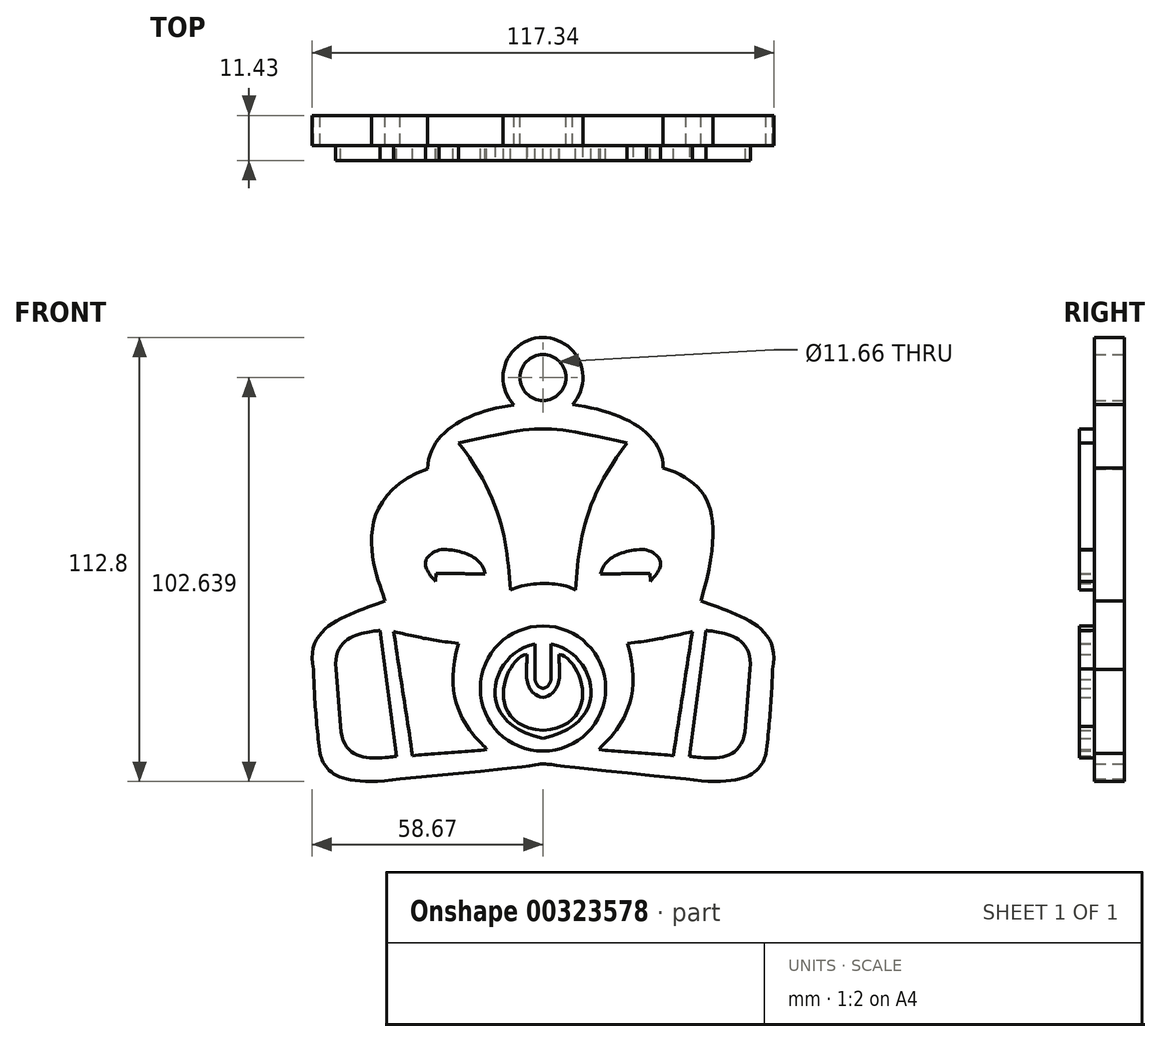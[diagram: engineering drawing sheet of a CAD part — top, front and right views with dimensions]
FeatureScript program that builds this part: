
annotation { "Feature Type Name" : "Feature", "Feature Type Description" : "" }
export const myFeature = defineFeature(function(context is Context, id is Id, definition is map)
    precondition{}
    {
        {
            var Q0;
            Q0=qCreatedBy(makeId("Front.planeOp"),FACE);
            var sketch = newSketch(context, id + "F0", { "sketchPlane" : qUnion([Q0])});
            skFitSpline(sketch, "E0", {"points": [v(-40.16, -4.93) * mm, v(-29.28, 28.6) * mm], "startDerivative": vector(-4.08, 14.8) * mm, "endDerivative": vector(66.61, 24.47) * mm});
            skFitSpline(sketch, "E1", {"points": [v(-29.28, 28.6) * mm, v(30.53, 28.82) * mm], "startDerivative": vector(1.44, 68.84) * mm, "endDerivative": vector(-0.6, -63.84) * mm});
            skFitSpline(sketch, "E2", {"points": [v(30.53, 28.82) * mm, v(40.16, -4.93) * mm], "startDerivative": vector(36.03, -11.56) * mm, "endDerivative": vector(-19.45, -66.97) * mm});
            skFitSpline(sketch, "E3", {"points": [v(-40.16, -4.93) * mm, v(-58.33, -22.39) * mm], "startDerivative": vector(-21.75, -9.52) * mm, "endDerivative": vector(7.92, -36) * mm});
            skFitSpline(sketch, "E4", {"points": [v(-56.66, -43.75) * mm, v(-58.33, -22.39) * mm], "startDerivative": vector(-2.72, 21.98) * mm, "endDerivative": vector(-0.72, 22.32) * mm});
            skFitSpline(sketch, "E5", {"points": [v(-56.66, -43.75) * mm, v(-36.3, -50.25) * mm], "startDerivative": vector(3.4, -12.91) * mm, "endDerivative": vector(48.26, 6.8) * mm});
            skFitSpline(sketch, "E6.MirrorCS", {"points": [v(56.66, -43.75) * mm, v(58.33, -22.39) * mm], "startDerivative": vector(2.72, 21.98) * mm, "endDerivative": vector(0.72, 22.32) * mm});
            skFitSpline(sketch, "E7.MirrorCS", {"points": [v(40.16, -4.93) * mm, v(58.33, -22.39) * mm], "startDerivative": vector(21.75, -9.52) * mm, "endDerivative": vector(-7.92, -36) * mm});
            skFitSpline(sketch, "E8.MirrorCS", {"points": [v(56.66, -43.75) * mm, v(36.3, -50.25) * mm], "startDerivative": vector(-3.4, -12.91) * mm, "endDerivative": vector(-48.26, 6.8) * mm});
            skFitSpline(sketch, "E9", {"points": [v(-36.3, -50.25) * mm, v(0, -46.4) * mm, v(36.3, -50.25) * mm], "startDerivative": vector(202.74, 18.7) * mm, "endDerivative": vector(201.98, -20.2) * mm});
            skSolve(sketch);
        }
        {
            var Q0;
            Q0=qSketchRegion(id+"F0",true);
            extrude(context, id + "F1", {"entities" : qUnion([Q0]), "depth" : 7.62 * mm});
        }
        {
            var Q0;
            Q0=makeQuery(id+"F1.opExtrude","CAP_FACE",FACE,{"disambiguationData":[OSD([sQuery(id+"F0.wireOp",EDGE,"E0"),sQuery(id+"F0.wireOp",EDGE,"E1"),sQuery(id+"F0.wireOp",EDGE,"E2"),sQuery(id+"F0.wireOp",EDGE,"E3"),sQuery(id+"F0.wireOp",EDGE,"E4"),sQuery(id+"F0.wireOp",EDGE,"E5"),sQuery(id+"F0.wireOp",EDGE,"E6.MirrorCS"),sQuery(id+"F0.wireOp",EDGE,"E7.MirrorCS"),sQuery(id+"F0.wireOp",EDGE,"E8.MirrorCS"),sQuery(id+"F0.wireOp",EDGE,"E9")])],"isStart":false});
            var sketch = newSketch(context, id + "F2", { "sketchPlane" : qUnion([Q0])});
            skFitSpline(sketch, "E10", {"points": [v(-8.3, -2.17) * mm, v(-21.4, 35.12) * mm], "startDerivative": vector(-2.34, 34.98) * mm, "endDerivative": vector(-33.95, 43.65) * mm});
            skFitSpline(sketch, "E11.MirrorCS", {"points": [v(8.3, -2.17) * mm, v(21.4, 35.12) * mm], "startDerivative": vector(2.34, 34.98) * mm, "endDerivative": vector(33.95, 43.65) * mm});
            skFitSpline(sketch, "E12", {"points": [v(-21.4, 35.12) * mm, v(21.4, 35.12) * mm], "startDerivative": vector(64.2, 14.53) * mm, "endDerivative": vector(64.2, -14.53) * mm});
            skFitSpline(sketch, "E13", {"points": [v(-8.3, -2.17) * mm, v(8.3, -2.17) * mm], "startDerivative": vector(15.24, 6.52) * mm, "endDerivative": vector(12.2, -6.52) * mm});
            skFitSpline(sketch, "E14", {"points": [v(-37.93, -12.75) * mm, v(-33.13, -44.31) * mm], "startDerivative": vector(4.8, -31.93) * mm, "endDerivative": vector(4.8, -31.93) * mm});
            skFitSpline(sketch, "E15", {"points": [v(-33.13, -44.31) * mm, v(-14.28, -42.75) * mm], "startDerivative": vector(16.8, 1.92) * mm, "endDerivative": vector(16.8, 1.92) * mm});
            skFitSpline(sketch, "E16", {"points": [v(-37.93, -12.75) * mm, v(-21.48, -15.75) * mm], "startDerivative": vector(18.72, -4.32) * mm, "endDerivative": vector(21.6, -2.16) * mm});
            skFitSpline(sketch, "E17", {"points": [v(-14.28, -42.75) * mm, v(-21.48, -15.75) * mm], "startDerivative": vector(-3.24, 6.12) * mm, "endDerivative": vector(15.84, 54.01) * mm});
            skFitSpline(sketch, "E18.MirrorCS", {"points": [v(37.93, -12.75) * mm, v(33.13, -44.31) * mm], "startDerivative": vector(-4.8, -31.93) * mm, "endDerivative": vector(-4.8, -31.93) * mm});
            skFitSpline(sketch, "E19.MirrorCS", {"points": [v(37.93, -12.75) * mm, v(21.48, -15.75) * mm], "startDerivative": vector(-18.72, -4.32) * mm, "endDerivative": vector(-21.6, -2.16) * mm});
            skFitSpline(sketch, "E20.MirrorCS", {"points": [v(14.28, -42.75) * mm, v(21.48, -15.75) * mm], "startDerivative": vector(3.24, 6.12) * mm, "endDerivative": vector(-15.84, 54.01) * mm});
            skFitSpline(sketch, "E21.MirrorCS", {"points": [v(33.13, -44.31) * mm, v(14.28, -42.75) * mm], "startDerivative": vector(-16.8, 1.92) * mm, "endDerivative": vector(-16.8, 1.92) * mm});
            skCircle(sketch, "E22", {"center": v(0, -27.23) * mm, "radius": 15.9 * mm});
            skFitSpline(sketch, "E23", {"points": [v(-2.08, -15.9) * mm, v(0, -39.95) * mm], "startDerivative": vector(-32.37, -5.93) * mm, "endDerivative": vector(56.75, -12.7) * mm});
            skFitSpline(sketch, "E24.MirrorCS", {"points": [v(2.08, -15.9) * mm, v(0, -39.95) * mm], "startDerivative": vector(32.37, -5.93) * mm, "endDerivative": vector(-56.75, -12.7) * mm});
            skFitSpline(sketch, "E25", {"points": [v(-27.26, 0) * mm, v(-26.36, 8) * mm], "startDerivative": vector(-11.06, 11.33) * mm, "endDerivative": vector(13.49, 5.4) * mm});
            skFitSpline(sketch, "E26", {"points": [v(-26.36, 8) * mm, v(-14.67, 1.89) * mm], "startDerivative": vector(14.03, 1.08) * mm, "endDerivative": vector(2.43, -14.03) * mm});
            skFitSpline(sketch, "E27", {"points": [v(-27.17, 1.98) * mm, v(-14.67, 1.89) * mm], "startDerivative": vector(11.42, -0.18) * mm, "endDerivative": vector(11.42, -0.18) * mm});
            skFitSpline(sketch, "E28", {"points": [v(-27.26, 0) * mm, v(-27.17, 1.98) * mm], "startDerivative": vector(0.09, 1.98) * mm, "endDerivative": vector(0.09, 1.98) * mm});
            skFitSpline(sketch, "E29.MirrorCS", {"points": [v(27.17, 1.98) * mm, v(14.67, 1.89) * mm], "startDerivative": vector(-11.42, -0.18) * mm, "endDerivative": vector(-11.42, -0.18) * mm});
            skFitSpline(sketch, "E30.MirrorCS", {"points": [v(27.26, 0) * mm, v(26.36, 8) * mm], "startDerivative": vector(11.06, 11.33) * mm, "endDerivative": vector(-13.49, 5.4) * mm});
            skFitSpline(sketch, "E31.MirrorCS", {"points": [v(26.36, 8) * mm, v(14.67, 1.89) * mm], "startDerivative": vector(-14.03, 1.08) * mm, "endDerivative": vector(-2.43, -14.03) * mm});
            skFitSpline(sketch, "E32.MirrorCS", {"points": [v(27.26, 0) * mm, v(27.17, 1.98) * mm], "startDerivative": vector(-0.09, 1.98) * mm, "endDerivative": vector(-0.09, 1.98) * mm});
            skFitSpline(sketch, "E33", {"points": [v(-4.05, -18.57) * mm, v(0, -37.94) * mm], "startDerivative": vector(-17, -2.38) * mm, "endDerivative": vector(47.17, -4.42) * mm});
            skFitSpline(sketch, "E34", {"points": [v(-4.05, -18.57) * mm, v(0, -29.56) * mm], "startDerivative": vector(0.34, -9.86) * mm, "endDerivative": vector(16.92, -4.08) * mm});
            skFitSpline(sketch, "E35.MirrorCS", {"points": [v(4.05, -18.57) * mm, v(0, -37.94) * mm], "startDerivative": vector(17, -2.38) * mm, "endDerivative": vector(-47.17, -4.42) * mm});
            skFitSpline(sketch, "E36.MirrorCS", {"points": [v(4.05, -18.57) * mm, v(0, -29.56) * mm], "startDerivative": vector(-0.34, -9.86) * mm, "endDerivative": vector(-16.92, -4.08) * mm});
            skFitSpline(sketch, "E37", {"points": [v(-41.44, -12.42) * mm, v(-37.27, -44.47) * mm], "startDerivative": vector(4.18, -32.06) * mm, "endDerivative": vector(4.18, -32.06) * mm});
            skFitSpline(sketch, "E38", {"points": [v(-41.44, -12.42) * mm, v(-52.62, -22.24) * mm], "startDerivative": vector(-4.45, -1.62) * mm, "endDerivative": vector(2.73, -29.44) * mm});
            skFitSpline(sketch, "E39", {"points": [v(-37.27, -44.47) * mm, v(-51.41, -36.92) * mm], "startDerivative": vector(-8.9, -0.4) * mm, "endDerivative": vector(-1.27, 31.67) * mm});
            skFitSpline(sketch, "E40", {"points": [v(-52.62, -22.24) * mm, v(-51.41, -36.92) * mm], "startDerivative": vector(1.21, -14.68) * mm, "endDerivative": vector(1.21, -14.68) * mm});
            skFitSpline(sketch, "E41", {"points": [v(-2.08, -15.9) * mm, v(-2.08, -24.94) * mm], "startDerivative": vector(0, -8.43) * mm, "endDerivative": vector(0, -8.43) * mm});
            skFitSpline(sketch, "E42", {"points": [v(0, -27.23) * mm, v(-2.08, -24.94) * mm], "startDerivative": vector(-3.28, 1.03) * mm, "endDerivative": vector(-1.66, 5) * mm});
            skFitSpline(sketch, "E43.MirrorCS", {"points": [v(37.27, -44.47) * mm, v(51.41, -36.92) * mm], "startDerivative": vector(8.9, -0.4) * mm, "endDerivative": vector(1.27, 31.67) * mm});
            skFitSpline(sketch, "E44.MirrorCS", {"points": [v(52.62, -22.24) * mm, v(51.41, -36.92) * mm], "startDerivative": vector(-1.21, -14.68) * mm, "endDerivative": vector(-1.21, -14.68) * mm});
            skFitSpline(sketch, "E45.MirrorCS", {"points": [v(41.44, -12.42) * mm, v(52.62, -22.24) * mm], "startDerivative": vector(4.45, -1.62) * mm, "endDerivative": vector(-2.73, -29.44) * mm});
            skFitSpline(sketch, "E46.MirrorCS", {"points": [v(41.44, -12.42) * mm, v(37.27, -44.47) * mm], "startDerivative": vector(-4.18, -32.06) * mm, "endDerivative": vector(-4.18, -32.06) * mm});
            skFitSpline(sketch, "E47.MirrorCS", {"points": [v(2.08, -15.9) * mm, v(2.08, -24.94) * mm], "startDerivative": vector(0, -8.43) * mm, "endDerivative": vector(0, -8.43) * mm});
            skFitSpline(sketch, "E48.MirrorCS", {"points": [v(0, -27.23) * mm, v(2.08, -24.94) * mm], "startDerivative": vector(3.28, 1.03) * mm, "endDerivative": vector(1.66, 5) * mm});
            skSolve(sketch);
        }
        {
            var Q0;
            Q0=qSketchRegion(id+"F2",true);
            var Q1;
            Q1=makeQuery(id+"F2.imprint","IMPRINT",FACE,{"disambiguationData":[TD([[makeQuery(id+"F2.imprint","IMPRINT",EDGE,{"derivedFrom":sQuery(id+"F2.wireOp",EDGE,"E33")}),1.0]])]});
            extrude(context, id + "F3", {"entities" : qUnion([Q0, Q1]), "operationType" : NewBodyOperationType.ADD, "depth" : 3.8 * mm});
        }
        {
            var Q0;
            Q0=qCreatedBy(makeId("Front.planeOp"),FACE);
            var sketch = newSketch(context, id + "F4", { "sketchPlane" : qUnion([Q0])});
            skCircle(sketch, "E49", {"center": v(0, 51.78) * mm, "radius": 10.16 * mm});
            skCircle(sketch, "E50", {"center": v(0, 51.78) * mm, "radius": 5.83 * mm});
            skSolve(sketch);
        }
        {
            var Q0;
            Q0=qSketchRegion(id+"F4",true);
            extrude(context, id + "F5", {"entities" : qUnion([Q0]), "operationType" : NewBodyOperationType.ADD, "depth" : 7.62 * mm});
        }
    });
